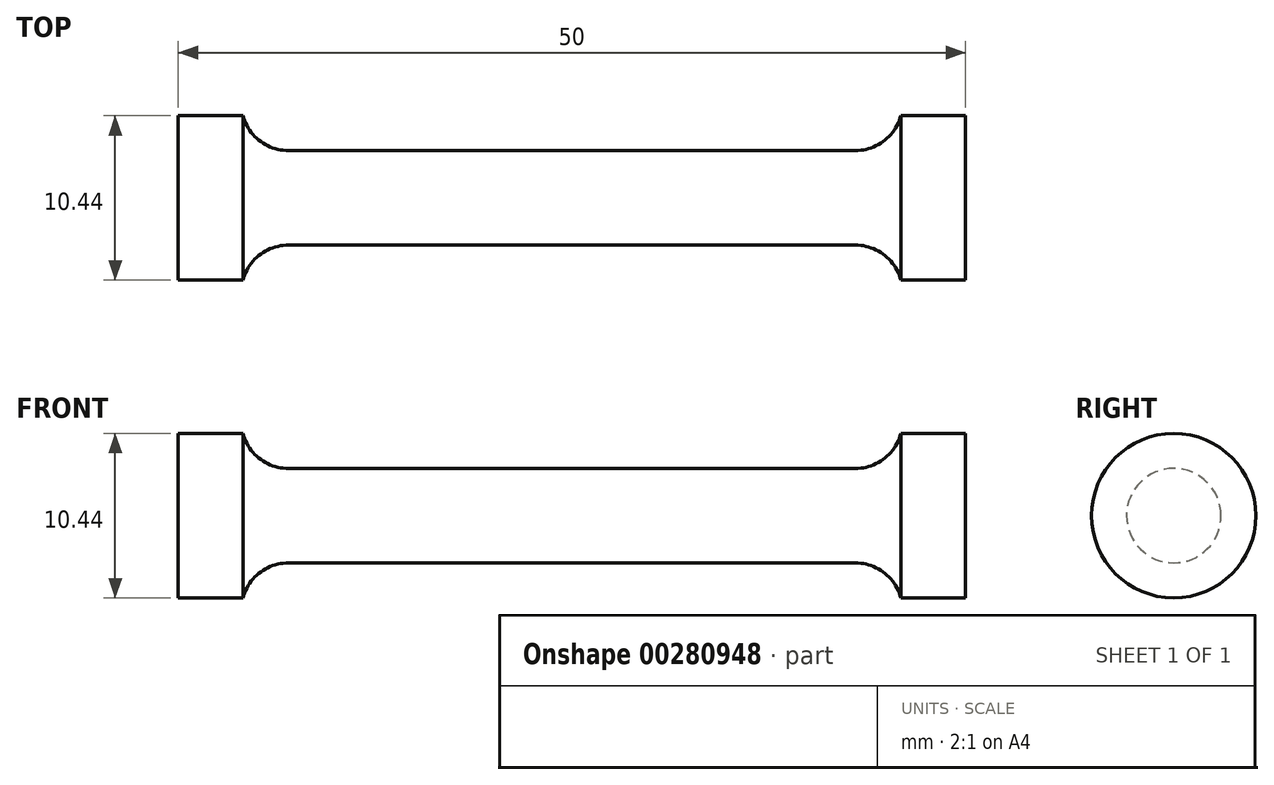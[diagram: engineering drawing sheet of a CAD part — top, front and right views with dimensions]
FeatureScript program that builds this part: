
annotation { "Feature Type Name" : "Feature", "Feature Type Description" : "" }
export const myFeature = defineFeature(function(context is Context, id is Id, definition is map)
    precondition{}
    {
        {
            var Q0;
            Q0=qCreatedBy(makeId("Front.planeOp"),FACE);
            var sketch = newSketch(context, id + "F0", { "sketchPlane" : qUnion([Q0])});
            skLineSegment(sketch, "E0", {"start": v(0, 3) * mm, "end": v(18, 3) * mm});
            skArc(sketch, "E1", {"start": v(18, 3) * mm, "mid": v(19.83, 3.62) * mm, "end": v(20.9, 5.22) * mm});
            skLineSegment(sketch, "E2", {"start": v(20.9, 5.22) * mm, "end": v(25, 5.22) * mm});
            skLineSegment(sketch, "E3", {"start": v(25, 5.22) * mm, "end": v(25, 0) * mm});
            skLineSegment(sketch, "E4", {"start": v(25, 0) * mm, "end": v(0, 0) * mm});
            skLineSegment(sketch, "E5.MirrorCS", {"start": v(0, 3) * mm, "end": v(-18, 3) * mm});
            skLineSegment(sketch, "E6.MirrorCS", {"start": v(-25, 0) * mm, "end": v(0, 0) * mm});
            skLineSegment(sketch, "E7.MirrorCS", {"start": v(-20.9, 5.22) * mm, "end": v(-25, 5.22) * mm});
            skLineSegment(sketch, "E8.MirrorCS", {"start": v(-25, 5.22) * mm, "end": v(-25, 0) * mm});
            skArc(sketch, "E9.MirrorCS", {"start": v(-18, 3) * mm, "mid": v(-19.83, 3.62) * mm, "end": v(-20.9, 5.22) * mm});
            skSolve(sketch);
        }
        {
            var Q0;
            Q0=makeQuery(id+"F0.imprint","IMPRINT",FACE,{"disambiguationData":[TD([[makeQuery(id+"F0.imprint","IMPRINT",EDGE,{"derivedFrom":sQuery(id+"F0.wireOp",EDGE,"E0")}),-1.0]])]});
            var Q1;
            Q1=sQuery(id+"F0.wireOp",EDGE,"E6.MirrorCS");
            revolve(context, id + "F1", {"entities" : qUnion([Q0]), "axis" : qUnion([Q1]), "revolveType" : RevolveType.FULL});
        }
    });
